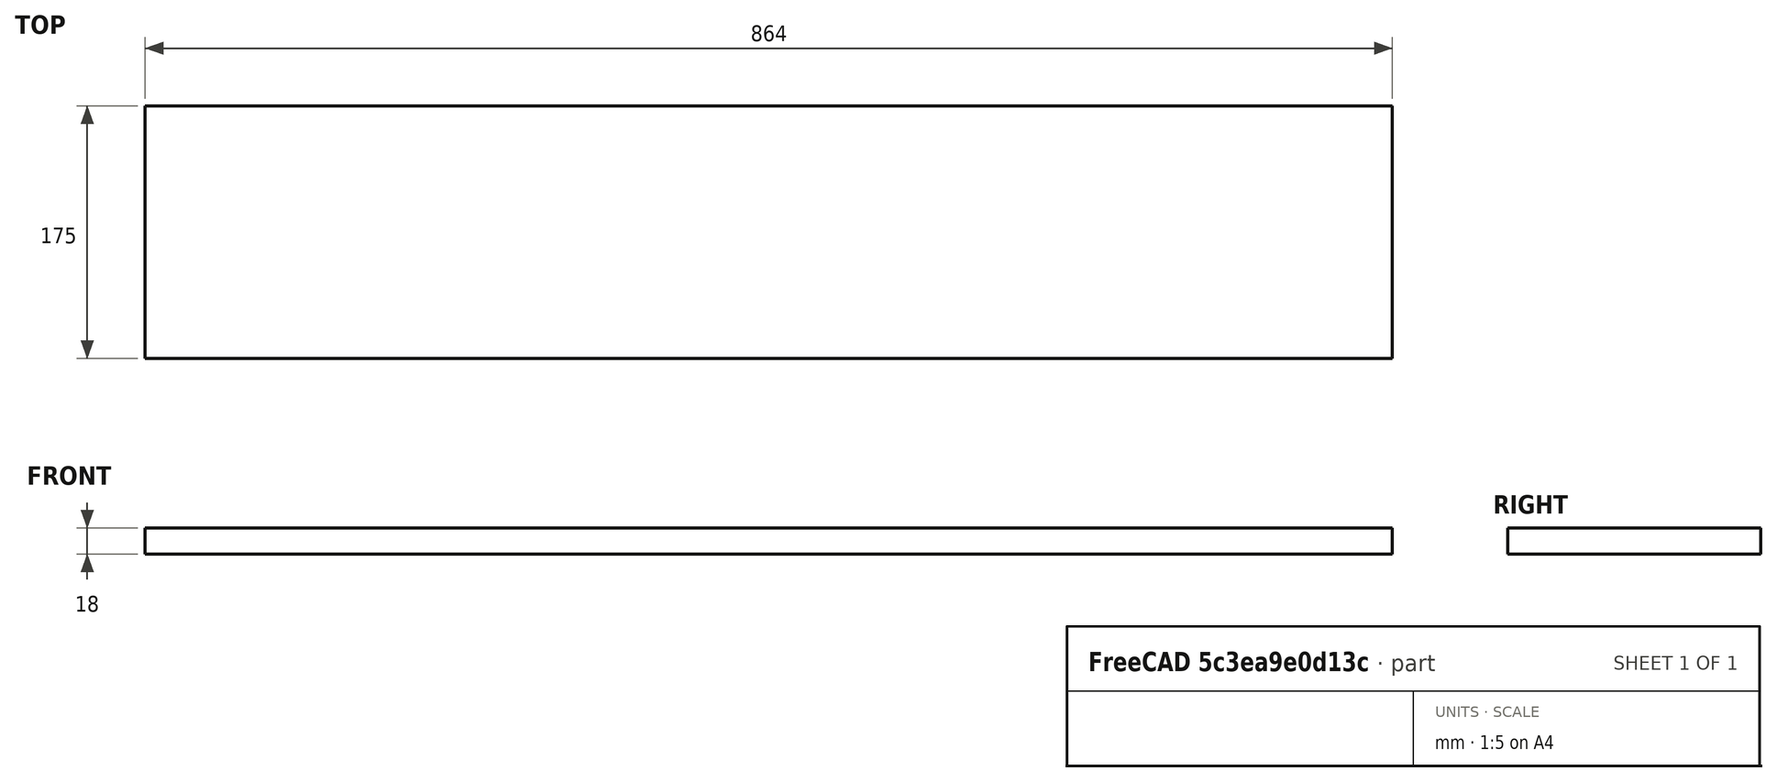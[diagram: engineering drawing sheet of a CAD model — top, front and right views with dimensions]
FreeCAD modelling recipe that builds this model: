
FCSTD DOCUMENT  (FreeCAD 1.0R39109 (Git))
Label: 13_shelf_sides_and_middle
License: All rights reserved
LicenseURL: http://en.wikipedia.org/wiki/All_rights_reserved
objects: Spreadsheet::Sheet×1, Sketcher::SketchObject×1, PartDesign::Pad×1, PartDesign::Body×1
note: 6 computed .brp shape members not serialized (recipe doc carries the construction recipe); baked Part::Feature solids carry a one-line shape summary decoded from their .brp

FEATURE [Spreadsheet::Sheet] Spreadsheet
  cells = A2='length; B2(length)=864; A3='width; B3(width)=175; A4='height; B4(height)=18
FEATURE [Sketcher::SketchObject] Sketch
  ArcFitTolerance = 0
  AttachmentSupport = -> [XY_Plane]
  FullyConstrained = true
  MakeInternals = false
  MapMode = 5
  expr: Constraints[11] = Spreadsheet.length
  expr: Constraints[12] = Spreadsheet.width
  sketch-geometry (5):
    g0: LineSegment StartX=-432 StartY=87.5 StartZ=0 EndX=432 EndY=87.5 EndZ=0
    g1: LineSegment StartX=432 StartY=87.5 StartZ=0 EndX=432 EndY=-87.5 EndZ=0
    g2: LineSegment StartX=432 StartY=-87.5 StartZ=0 EndX=-432 EndY=-87.5 EndZ=0
    g3: LineSegment StartX=-432 StartY=-87.5 StartZ=0 EndX=-432 EndY=87.5 EndZ=0
    g4: LineSegment [constr] StartX=-432 StartY=87.5 StartZ=0 EndX=432 EndY=-87.5 EndZ=0
  constraints (13):
    c: Coincident(g0,g1)
    c: Coincident(g1,g2)
    c: Coincident(g2,g3)
    c: Coincident(g3,g0)
    c: Horizontal(g0)
    c: Horizontal(g2)
    c: Vertical(g1)
    c: Vertical(g3)
    c: Coincident(g4,g1)
    c: Coincident(g0,g4)
    c: Symmetric(g0,g1,g-1)
    c: Distance(g0,g0) = 864
    c: Distance(g0,g2) = 175
FEATURE [PartDesign::Pad] Pad
  Direction = (0,0,1)
  Length = 18
  Length2 = 10
  Profile = -> Sketch
  ReferenceAxis = -> Sketch [N_Axis]
  Suppressed = false
  Type = 0
  expr: Length = Spreadsheet.height
FEATURE [PartDesign::Body] Body
  AllowCompound = false
  Group = -> [Sketch,Pad]
  Origin = -> Origin
  Tip = -> Pad
